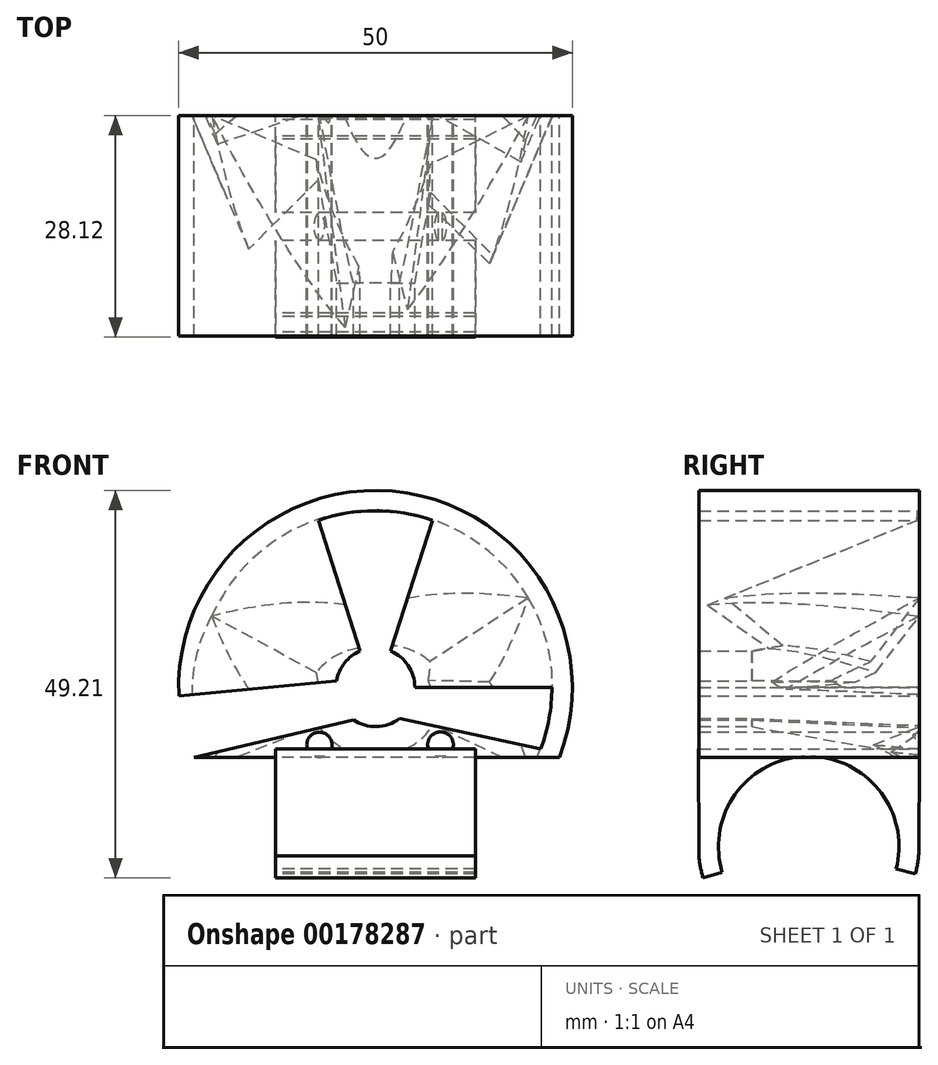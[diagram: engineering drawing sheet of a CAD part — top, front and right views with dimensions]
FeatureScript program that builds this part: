
annotation { "Feature Type Name" : "Feature", "Feature Type Description" : "" }
export const myFeature = defineFeature(function(context is Context, id is Id, definition is map)
    precondition{}
    {
        {
            var Q0;
            Q0=qCreatedBy(makeId("Front.planeOp"),FACE);
            var sketch = newSketch(context, id + "F0", { "sketchPlane" : qUnion([Q0])});
            skPoint(sketch, "E0.middle", {"position": v(25, 0) * mm});
            skPoint(sketch, "E1.middle", {"position": v(0, -9.45) * mm});
            skArc(sketch, "E2", {"start": v(23.36, -8.91) * mm, "mid": v(3.99, 24.68) * mm, "end": v(-24.98, -1.1) * mm});
            skLineSegment(sketch, "E3", {"start": v(-23.36, -8.91) * mm, "end": v(-23.01, -8.91) * mm});
            skLineSegment(sketch, "E4", {"start": v(20.06, -10) * mm, "end": v(20.06, -10) * mm});
            skLineSegment(sketch, "E5", {"start": v(-23.01, -8.91) * mm, "end": v(-2.81, -4.13) * mm});
            skLineSegment(sketch, "E6", {"start": v(21, -7.84) * mm, "end": v(3.06, -3.96) * mm});
            skLineSegment(sketch, "E7", {"start": v(-22.4, -0.85) * mm, "end": v(-24.98, -1.1) * mm});
            skLineSegment(sketch, "E8", {"start": v(-20.78, -8.38) * mm, "end": v(-20.78, -8.38) * mm});
            skLineSegment(sketch, "E9", {"start": v(-23.4, -8.8) * mm, "end": v(-23.4, -8.8) * mm});
            skLineSegment(sketch, "E10", {"start": v(-7.22, 21.22) * mm, "end": v(-7.22, 21.22) * mm});
            skArc(sketch, "E11", {"start": v(-0.37, 22.4) * mm, "mid": v(-3.84, 22.08) * mm, "end": v(-7.22, 21.22) * mm});
            skLineSegment(sketch, "E12", {"start": v(-7.22, 21.22) * mm, "end": v(-1.94, 4.6) * mm});
            skArc(sketch, "E13", {"start": v(7.22, 21.22) * mm, "mid": v(3.48, 22.14) * mm, "end": v(-0.37, 22.4) * mm});
            skLineSegment(sketch, "E14", {"start": v(-22.4, -0.85) * mm, "end": v(-22.4, -0.85) * mm});
            skArc(sketch, "E15", {"start": v(21, -7.84) * mm, "mid": v(22.05, -3.98) * mm, "end": v(22.4, 0) * mm});
            skLineSegment(sketch, "E16", {"start": v(-1.31, -3.78) * mm, "end": v(-1.31, -3.78) * mm});
            skLineSegment(sketch, "E17", {"start": v(4, 0) * mm, "end": v(4, 0) * mm});
            skPoint(sketch, "E1.right.end.orphan", {"position": v(40.39, -8.91) * mm});
            skPoint(sketch, "E18.orphan", {"position": v(40.39, -10) * mm});
            skPoint(sketch, "E1.left.end.orphan", {"position": v(-40.39, -8.91) * mm});
            skPoint(sketch, "E1.left.start.orphan", {"position": v(-40.39, -10) * mm});
            skLineSegment(sketch, "E19", {"start": v(-23.01, -8.91) * mm, "end": v(23.36, -8.91) * mm});
            skPoint(sketch, "E20", {"position": v(-1.94, 4.6) * mm});
            skPoint(sketch, "E21", {"position": v(-2.81, -4.13) * mm});
            skPoint(sketch, "E22", {"position": v(3.06, -3.96) * mm});
            skPoint(sketch, "E23", {"position": v(5, 0) * mm});
            skPoint(sketch, "E24", {"position": v(1.94, 4.6) * mm});
            skArc(sketch, "E25", {"start": v(-2.81, -4.13) * mm, "mid": v(0.15, -5) * mm, "end": v(3.06, -3.96) * mm});
            skArc(sketch, "E26", {"start": v(-1.94, 4.6) * mm, "mid": v(-3.92, 3.1) * mm, "end": v(-4.93, 0.84) * mm});
            skArc(sketch, "E27", {"start": v(5, 0) * mm, "mid": v(4.17, 2.76) * mm, "end": v(1.94, 4.6) * mm});
            skLineSegment(sketch, "E28", {"start": v(-4.93, 0.84) * mm, "end": v(-22.4, -0.85) * mm});
            skLineSegment(sketch, "E29", {"start": v(1.64, -3.65) * mm, "end": v(1.64, -3.65) * mm});
            skLineSegment(sketch, "E30", {"start": v(5, 0) * mm, "end": v(22.4, 0) * mm});
            skLineSegment(sketch, "E31", {"start": v(1.64, 3.65) * mm, "end": v(1.64, 3.65) * mm});
            skLineSegment(sketch, "E32", {"start": v(1.94, 4.6) * mm, "end": v(7.22, 21.22) * mm});
            skSolve(sketch);
        }
        {
            var Q0;
            Q0=makeQuery(id+"F0.imprint","IMPRINT",FACE,{"disambiguationData":[TD([[makeQuery(id+"F0.imprint","IMPRINT",EDGE,{"derivedFrom":sQuery(id+"F0.wireOp",EDGE,"E2")}),1.0]])]});
            extrude(context, id + "F1", {"entities" : qUnion([Q0]), "depth" : 28 * mm});
        }
        {
            var Q0;
            Q0=qCreatedBy(makeId("Front.planeOp"),FACE);
            var sketch = newSketch(context, id + "F2", { "sketchPlane" : qUnion([Q0])});
            skLineSegment(sketch, "E33", {"start": v(4.98, 0) * mm, "end": v(15.3, 0) * mm});
            skArc(sketch, "E34", {"start": v(19.43, 11.36) * mm, "mid": v(-1.4, 22.47) * mm, "end": v(-20.8, 9.04) * mm});
            skArc(sketch, "E35", {"start": v(19.63, -10.6) * mm, "mid": v(22.48, 0.4) * mm, "end": v(19.43, 11.36) * mm});
            skArc(sketch, "E36", {"start": v(-20.8, 9.04) * mm, "mid": v(-23.3, -0.56) * mm, "end": v(-20.8, -10.16) * mm});
            skLineSegment(sketch, "E37", {"start": v(19.43, 11.36) * mm, "end": v(0, -6.84) * mm});
            skLineSegment(sketch, "E38", {"start": v(0, -6.84) * mm, "end": v(-20.8, 9.04) * mm});
            skLineSegment(sketch, "E39", {"start": v(-20.8, -10.16) * mm, "end": v(4.98, 0) * mm});
            skLineSegment(sketch, "E40", {"start": v(4.98, 0) * mm, "end": v(-20.8, 9.04) * mm});
            skLineSegment(sketch, "E41", {"start": v(19.63, -10.6) * mm, "end": v(-5, 1.15) * mm});
            skLineSegment(sketch, "E42", {"start": v(-5, 1.15) * mm, "end": v(19.43, 11.36) * mm});
            skSolve(sketch);
        }
        {
            var Q0;
            Q0=makeQuery(id+"F2.imprint","IMPRINT",FACE,{"disambiguationData":[TD([[makeQuery(id+"F2.imprint","IMPRINT",EDGE,{"derivedFrom":sQuery(id+"F2.wireOp",EDGE,"E34")}),1.0]])]});
            var Q1;
            {var subQ1=sQuery(id+"F2.wireOp",EDGE,"E33");var subQ3=sQuery(id+"F2.wireOp",EDGE,"E37");var subQ4=makeQuery(id+"F2.imprint","INTERSECT",VERTEX,{"derivedFrom":[subQ1,subQ3]});Q1=makeQuery(id+"F2.imprint","IMPRINT",FACE,{"disambiguationData":[TD([[makeQuery(id+"F2.imprint","IMPRINT",EDGE,{"disambiguationData":[TD([[subQ4,1.0]])],"derivedFrom":subQ1}),1.0]])]});}
            var Q2;
            {var subQ1=sQuery(id+"F2.wireOp",EDGE,"E33");var subQ3=sQuery(id+"F2.wireOp",EDGE,"E37");var subQ4=makeQuery(id+"F2.imprint","INTERSECT",VERTEX,{"derivedFrom":[subQ1,subQ3]});Q2=makeQuery(id+"F2.imprint","IMPRINT",FACE,{"disambiguationData":[TD([[makeQuery(id+"F2.imprint","IMPRINT",EDGE,{"disambiguationData":[TD([[subQ4,-1.0]])],"derivedFrom":subQ3}),-1.0]])]});}
            var Q3;
            {var subQ0=sQuery(id+"F2.wireOp",EDGE,"E38");var subQ1=sQuery(id+"F2.wireOp",EDGE,"E37");var subQ2=makeQuery(id+"F2.imprint","INTERSECT",VERTEX,{"derivedFrom":[subQ1,subQ0]});Q3=makeQuery(id+"F2.imprint","IMPRINT",FACE,{"disambiguationData":[TD([[makeQuery(id+"F2.imprint","IMPRINT",EDGE,{"disambiguationData":[TD([[subQ2,1.0]])],"derivedFrom":subQ1}),-1.0]])]});}
            var Q4;
            {var subQ3=sQuery(id+"F2.wireOp",EDGE,"E41");var subQ5=sQuery(id+"F2.wireOp",EDGE,"E42");var subQ6=makeQuery(id+"F2.imprint","INTERSECT",VERTEX,{"derivedFrom":[subQ3,subQ5]});Q4=makeQuery(id+"F2.imprint","IMPRINT",FACE,{"disambiguationData":[TD([[makeQuery(id+"F2.imprint","IMPRINT",EDGE,{"disambiguationData":[TD([[subQ6,1.0]])],"derivedFrom":subQ3}),-1.0]])]});}
            var Q5;
            {var subQ1=sQuery(id+"F2.wireOp",EDGE,"E38");var subQ7=sQuery(id+"F2.wireOp",EDGE,"E39");var subQ9=makeQuery(id+"F2.imprint","INTERSECT",VERTEX,{"derivedFrom":[subQ1,subQ7]});Q5=makeQuery(id+"F2.imprint","IMPRINT",FACE,{"disambiguationData":[TD([[makeQuery(id+"F2.imprint","IMPRINT",EDGE,{"disambiguationData":[TD([[subQ9,-1.0]])],"derivedFrom":subQ7}),1.0]])]});}
            extrude(context, id + "F3", {"entities" : qUnion([Q0, Q1, Q2, Q3, Q4, Q5]), "operationType" : NewBodyOperationType.REMOVE, "depth" : 28 * mm, "hasDraft" : true, "draftAngle" : 23 * degree, "draftPullDirection" : true});
        }
        {
            var Q0;
            Q0=qCreatedBy(makeId("Front.planeOp"),FACE);
            var sketch = newSketch(context, id + "F4", { "sketchPlane" : qUnion([Q0])});
            skCircle(sketch, "E43", {"center": v(8.26, -7.3) * mm, "radius": 1.63 * mm});
            skCircle(sketch, "E44", {"center": v(-7.12, -7.3) * mm, "radius": 1.6 * mm});
            skSolve(sketch);
        }
        {
            var Q0;
            Q0=makeQuery(id+"F4.imprint","IMPRINT",FACE,{"disambiguationData":[TD([[makeQuery(id+"F4.imprint","IMPRINT",EDGE,{"derivedFrom":sQuery(id+"F4.wireOp",EDGE,"E43")}),1.0]])]});
            var Q1;
            Q1=makeQuery(id+"F4.imprint","IMPRINT",FACE,{"disambiguationData":[TD([[makeQuery(id+"F4.imprint","IMPRINT",EDGE,{"derivedFrom":sQuery(id+"F4.wireOp",EDGE,"E44")}),1.0]])]});
            extrude(context, id + "F5", {"entities" : qUnion([Q0, Q1]), "operationType" : NewBodyOperationType.REMOVE, "endBound" : BoundingType.THROUGH_ALL, "depth" : 25.4 * mm});
        }
        {
            var Q0;
            Q0=qCreatedBy(makeId("Right.planeOp"),FACE);
            var sketch = newSketch(context, id + "F6", { "sketchPlane" : qUnion([Q0])});
            skLineSegment(sketch, "E45", {"start": v(-14.08, -20.23) * mm, "end": v(-13.98, -20.26) * mm});
            skArc(sketch, "E46", {"start": v(-2.98, -23.06) * mm, "mid": v(-14.3, -8.77) * mm, "end": v(-25.07, -23.49) * mm});
            skArc(sketch, "E47", {"start": v(-0.52, -23.68) * mm, "mid": v(-0.2, -22.02) * mm, "end": v(-0.08, -20.33) * mm});
            skLineSegment(sketch, "E48", {"start": v(-25.07, -23.49) * mm, "end": v(-27.5, -24.2) * mm});
            skArc(sketch, "E49", {"start": v(-28.04, -21.39) * mm, "mid": v(-27.85, -22.81) * mm, "end": v(-27.5, -24.2) * mm});
            skLineSegment(sketch, "E50", {"start": v(-2.98, -23.06) * mm, "end": v(-0.52, -23.68) * mm});
            skLineSegment(sketch, "E51", {"start": v(-28.12, -7.8) * mm, "end": v(0, -7.8) * mm});
            skLineSegment(sketch, "E52", {"start": v(0, -7.8) * mm, "end": v(-0.08, -20.33) * mm});
            skLineSegment(sketch, "E53", {"start": v(-28.12, -7.8) * mm, "end": v(-28.04, -21.39) * mm});
            skSolve(sketch);
        }
        {
            var Q0;
            {var subQ0=sQuery(id+"F2.wireOp",EDGE,"E36");Q0=makeQuery(id+"F2.imprint","IMPRINT",FACE,{"disambiguationData":[TD([[makeQuery(id+"F2.imprint","IMPRINT",EDGE,{"derivedFrom":subQ0}),1.0]])]});}
            var Q1;
            {var subQ1=sQuery(id+"F2.wireOp",EDGE,"E38");var subQ7=sQuery(id+"F2.wireOp",EDGE,"E39");var subQ9=makeQuery(id+"F2.imprint","INTERSECT",VERTEX,{"derivedFrom":[subQ1,subQ7]});Q1=makeQuery(id+"F2.imprint","IMPRINT",FACE,{"disambiguationData":[TD([[makeQuery(id+"F2.imprint","IMPRINT",EDGE,{"disambiguationData":[TD([[subQ9,-1.0]])],"derivedFrom":subQ7}),1.0]])]});}
            var Q2;
            {var subQ3=sQuery(id+"F2.wireOp",EDGE,"E41");var subQ5=sQuery(id+"F2.wireOp",EDGE,"E42");var subQ6=makeQuery(id+"F2.imprint","INTERSECT",VERTEX,{"derivedFrom":[subQ3,subQ5]});Q2=makeQuery(id+"F2.imprint","IMPRINT",FACE,{"disambiguationData":[TD([[makeQuery(id+"F2.imprint","IMPRINT",EDGE,{"disambiguationData":[TD([[subQ6,1.0]])],"derivedFrom":subQ3}),-1.0]])]});}
            extrude(context, id + "F7", {"entities" : qUnion([Q0, Q1, Q2]), "operationType" : NewBodyOperationType.REMOVE, "depth" : 28 * mm, "hasDraft" : true, "draftAngle" : 23 * degree, "draftPullDirection" : true});
        }
        {
            var Q0;
            {var subQ0=sQuery(id+"F2.wireOp",EDGE,"E35");Q0=makeQuery(id+"F2.imprint","IMPRINT",FACE,{"disambiguationData":[TD([[makeQuery(id+"F2.imprint","IMPRINT",EDGE,{"derivedFrom":subQ0}),1.0]])]});}
            var Q1;
            {var subQ1=sQuery(id+"F2.wireOp",EDGE,"E33");var subQ3=sQuery(id+"F2.wireOp",EDGE,"E37");var subQ4=makeQuery(id+"F2.imprint","INTERSECT",VERTEX,{"derivedFrom":[subQ1,subQ3]});Q1=makeQuery(id+"F2.imprint","IMPRINT",FACE,{"disambiguationData":[TD([[makeQuery(id+"F2.imprint","IMPRINT",EDGE,{"disambiguationData":[TD([[subQ4,1.0]])],"derivedFrom":subQ1}),1.0]])]});}
            var Q2;
            {var subQ3=sQuery(id+"F2.wireOp",EDGE,"E41");var subQ5=sQuery(id+"F2.wireOp",EDGE,"E42");var subQ6=makeQuery(id+"F2.imprint","INTERSECT",VERTEX,{"derivedFrom":[subQ3,subQ5]});Q2=makeQuery(id+"F2.imprint","IMPRINT",FACE,{"disambiguationData":[TD([[makeQuery(id+"F2.imprint","IMPRINT",EDGE,{"disambiguationData":[TD([[subQ6,1.0]])],"derivedFrom":subQ3}),-1.0]])]});}
            var Q3;
            {var subQ1=sQuery(id+"F2.wireOp",EDGE,"E33");var subQ3=sQuery(id+"F2.wireOp",EDGE,"E37");var subQ4=makeQuery(id+"F2.imprint","INTERSECT",VERTEX,{"derivedFrom":[subQ1,subQ3]});Q3=makeQuery(id+"F2.imprint","IMPRINT",FACE,{"disambiguationData":[TD([[makeQuery(id+"F2.imprint","IMPRINT",EDGE,{"disambiguationData":[TD([[subQ4,-1.0]])],"derivedFrom":subQ3}),-1.0]])]});}
            extrude(context, id + "F8", {"entities" : qUnion([Q0, Q1, Q2, Q3]), "operationType" : NewBodyOperationType.REMOVE, "depth" : 28 * mm, "hasDraft" : true, "draftAngle" : 23 * degree, "draftPullDirection" : true});
        }
        {
            var Q0;
            Q0=qCreatedBy(makeId("Front.planeOp"),FACE);
            var sketch = newSketch(context, id + "F9", { "sketchPlane" : qUnion([Q0])});
            skCircle(sketch, "E54", {"center": v(0, 0) * mm, "radius": 8.75 * mm});
            skSolve(sketch);
        }
        {
            var Q0;
            Q0=makeQuery(id+"F9.imprint","IMPRINT",FACE,{"disambiguationData":[TD([[makeQuery(id+"F9.imprint","IMPRINT",EDGE,{"derivedFrom":sQuery(id+"F9.wireOp",EDGE,"E54")}),1.0]])]});
            extrude(context, id + "F10", {"entities" : qUnion([Q0]), "operationType" : NewBodyOperationType.REMOVE, "depth" : 30 * mm, "hasDraft" : true, "draftAngle" : 10 * degree, "draftPullDirection" : true});
        }
        {
            var Q0;
            Q0=makeQuery(id+"F6.imprint","IMPRINT",FACE,{"disambiguationData":[TD([[makeQuery(id+"F6.imprint","IMPRINT",EDGE,{"derivedFrom":sQuery(id+"F6.wireOp",EDGE,"E46")}),-1.0]])]});
            extrude(context, id + "F11", {"entities" : qUnion([Q0]), "operationType" : NewBodyOperationType.ADD, "depth" : 25.4 * mm, "symmetric" : true});
        }
    });
